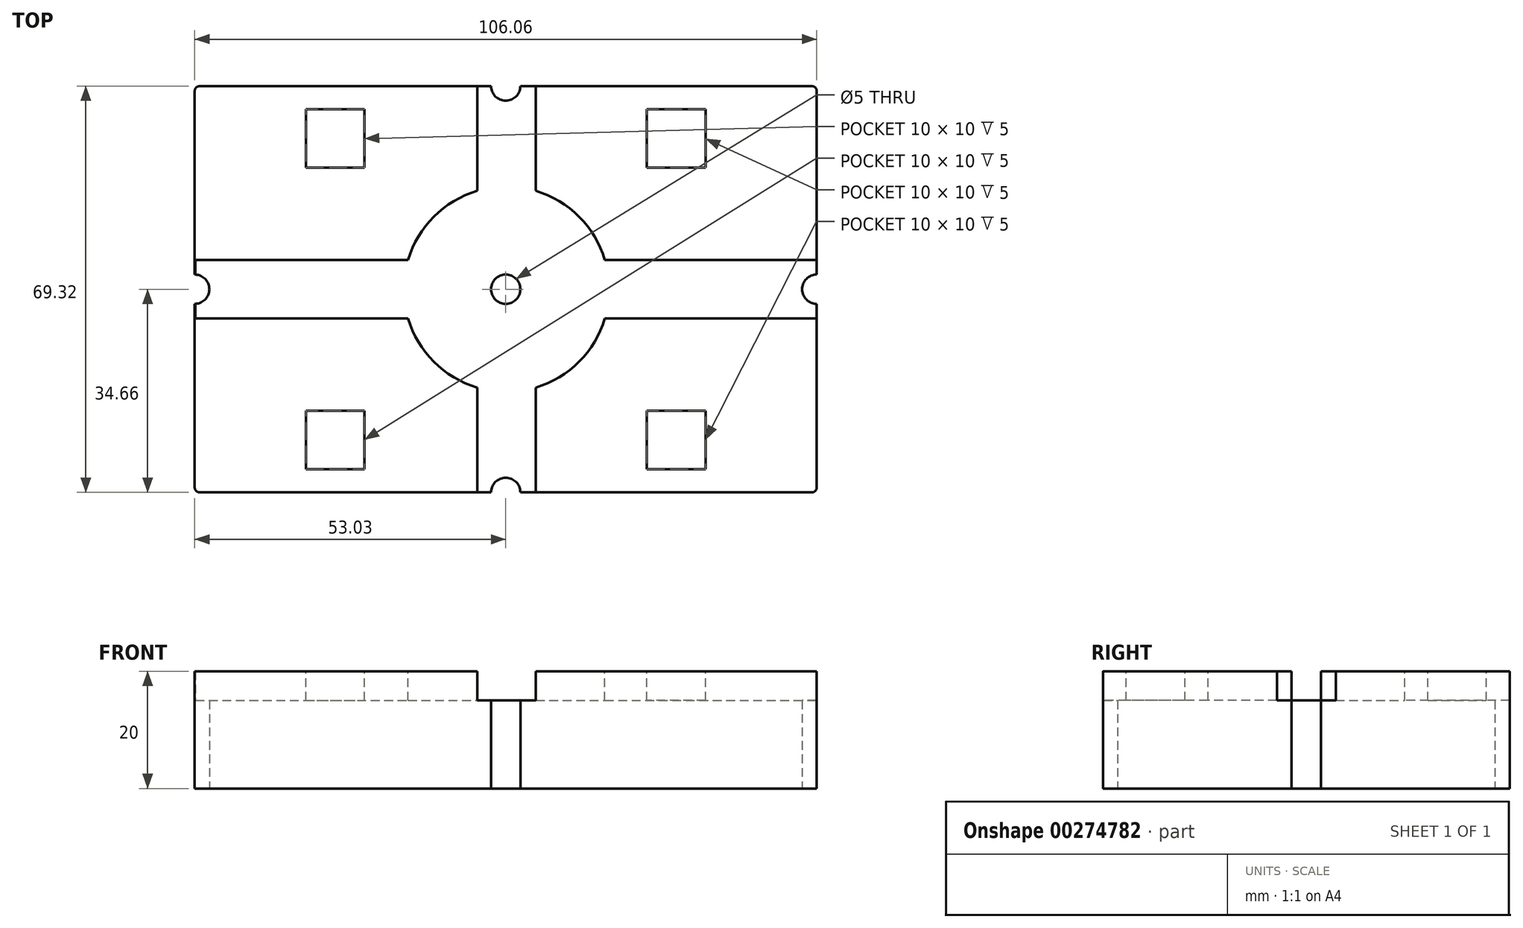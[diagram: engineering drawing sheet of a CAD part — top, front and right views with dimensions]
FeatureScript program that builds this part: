
annotation { "Feature Type Name" : "Feature", "Feature Type Description" : "" }
export const myFeature = defineFeature(function(context is Context, id is Id, definition is map)
    precondition{}
    {
        {
            var Q0;
            Q0=qCreatedBy(makeId("Top.planeOp"),FACE);
            var sketch = newSketch(context, id + "F0", { "sketchPlane" : qUnion([Q0])});
            skLineSegment(sketch, "E0.bottom", {"start": v(53.03, -34.66) * mm, "end": v(-53.03, -34.66) * mm});
            skLineSegment(sketch, "E0.top", {"start": v(53.03, 34.66) * mm, "end": v(-53.03, 34.66) * mm});
            skLineSegment(sketch, "E0.left", {"start": v(53.03, -34.66) * mm, "end": v(53.03, 34.66) * mm});
            skLineSegment(sketch, "E0.right", {"start": v(-53.03, -34.66) * mm, "end": v(-53.03, 34.66) * mm});
            skPoint(sketch, "E0.middle", {"position": v(0, 0) * mm});
            skLineSegment(sketch, "E1", {"start": v(-5, 0) * mm, "end": v(0, 0) * mm, "construction": true});
            skLineSegment(sketch, "E2.0", {"start": v(-53.03, -5) * mm, "end": v(-16.77, -5) * mm});
            skLineSegment(sketch, "E3.0", {"start": v(-53.03, 5) * mm, "end": v(-16.77, 5) * mm});
            skLineSegment(sketch, "E4", {"start": v(0, 5) * mm, "end": v(0, -5) * mm, "construction": true});
            skLineSegment(sketch, "E5.0", {"start": v(5, 34.66) * mm, "end": v(5, 16.77) * mm});
            skLineSegment(sketch, "E6.0", {"start": v(-5, 34.66) * mm, "end": v(-5, 16.77) * mm});
            skPoint(sketch, "E7.orphan", {"position": v(-53.03, 0) * mm});
            skLineSegment(sketch, "E8.trimOffspring", {"start": v(-5, -16.77) * mm, "end": v(-5, -34.66) * mm});
            skPoint(sketch, "E9.orphan", {"position": v(0, 34.66) * mm});
            skLineSegment(sketch, "E10.trimOffspring", {"start": v(5, -16.77) * mm, "end": v(5, -34.66) * mm});
            skLineSegment(sketch, "E11.trimOffspring", {"start": v(16.77, 5) * mm, "end": v(53.03, 5) * mm});
            skPoint(sketch, "E12.orphan", {"position": v(0, -34.66) * mm});
            skLineSegment(sketch, "E13.trimOffspring", {"start": v(16.77, -5) * mm, "end": v(53.03, -5) * mm});
            skPoint(sketch, "E14.orphan", {"position": v(53.03, 0) * mm});
            skCircle(sketch, "E15", {"center": v(0, 0) * mm, "radius": 17.5 * mm});
            skSolve(sketch);
        }
        {
            var Q0;
            {var subQ0=sQuery(id+"F0.wireOp",EDGE,"E5.0");Q0=makeQuery(id+"F0.imprint","IMPRINT",FACE,{"disambiguationData":[TD([[makeQuery(id+"F0.imprint","IMPRINT",EDGE,{"derivedFrom":subQ0}),1.0]])]});}
            var Q1;
            {var subQ0=sQuery(id+"F0.wireOp",EDGE,"E5.0");Q1=makeQuery(id+"F0.imprint","IMPRINT",FACE,{"disambiguationData":[TD([[makeQuery(id+"F0.imprint","IMPRINT",EDGE,{"derivedFrom":subQ0}),-1.0]])]});}
            var Q2;
            {var subQ1=sQuery(id+"F0.wireOp",EDGE,"E3.0");Q2=makeQuery(id+"F0.imprint","IMPRINT",FACE,{"disambiguationData":[TD([[makeQuery(id+"F0.imprint","IMPRINT",EDGE,{"derivedFrom":subQ1}),1.0]])]});}
            var Q3;
            {var subQ0=sQuery(id+"F0.wireOp",EDGE,"E2.0");Q3=makeQuery(id+"F0.imprint","IMPRINT",FACE,{"disambiguationData":[TD([[makeQuery(id+"F0.imprint","IMPRINT",EDGE,{"derivedFrom":subQ0}),-1.0]])]});}
            var Q4;
            {var subQ4=sQuery(id+"F0.wireOp",EDGE,"E10.trimOffspring");Q4=makeQuery(id+"F0.imprint","IMPRINT",FACE,{"disambiguationData":[TD([[makeQuery(id+"F0.imprint","IMPRINT",EDGE,{"derivedFrom":subQ4}),1.0]])]});}
            var Q5;
            {var subQ0=sQuery(id+"F0.wireOp",EDGE,"E11.trimOffspring");Q5=makeQuery(id+"F0.imprint","IMPRINT",FACE,{"disambiguationData":[TD([[makeQuery(id+"F0.imprint","IMPRINT",EDGE,{"derivedFrom":subQ0}),-1.0]])]});}
            var Q6;
            {var subQ0=sQuery(id+"F0.wireOp",EDGE,"E15");var subQ4=makeQuery(id+"F0.imprint","INTERSECT",VERTEX,{"derivedFrom":[sQuery(id+"F0.wireOp",EDGE,"E5.0"),subQ0]});Q6=makeQuery(id+"F0.imprint","IMPRINT",FACE,{"disambiguationData":[TD([[makeQuery(id+"F0.imprint","IMPRINT",EDGE,{"disambiguationData":[TD([[subQ4,1.0]])],"derivedFrom":subQ0}),1.0]])]});}
            var Q7;
            {var subQ0=sQuery(id+"F0.wireOp",EDGE,"E2.0");Q7=makeQuery(id+"F0.imprint","IMPRINT",FACE,{"disambiguationData":[TD([[makeQuery(id+"F0.imprint","IMPRINT",EDGE,{"derivedFrom":subQ0}),1.0]])]});}
            var Q8;
            {var subQ0=sQuery(id+"F0.wireOp",EDGE,"E8.trimOffspring");Q8=makeQuery(id+"F0.imprint","IMPRINT",FACE,{"disambiguationData":[TD([[makeQuery(id+"F0.imprint","IMPRINT",EDGE,{"derivedFrom":subQ0}),1.0]])]});}
            extrude(context, id + "F1", {"entities" : qUnion([Q0, Q1, Q2, Q3, Q4, Q5, Q6, Q7, Q8]), "depth" : 20 * mm});
        }
        {
            var Q0;
            Q0=makeQuery(id+"F1.opExtrude","CAP_FACE",FACE,{"disambiguationData":[OSD([sQuery(id+"F0.wireOp",EDGE,"E0.bottom"),sQuery(id+"F0.wireOp",EDGE,"E0.top"),sQuery(id+"F0.wireOp",EDGE,"E0.left"),sQuery(id+"F0.wireOp",EDGE,"E0.right")])],"isStart":false});
            var sketch = newSketch(context, id + "F2", { "sketchPlane" : qUnion([Q0])});
            skLineSegment(sketch, "E16.bottom", {"start": v(53.15, -34.66) * mm, "end": v(-52.9, -34.66) * mm});
            skLineSegment(sketch, "E16.top", {"start": v(53.15, 34.66) * mm, "end": v(-52.9, 34.66) * mm});
            skLineSegment(sketch, "E16.left", {"start": v(53.15, -34.66) * mm, "end": v(53.15, 34.66) * mm});
            skLineSegment(sketch, "E16.right", {"start": v(-52.9, -34.66) * mm, "end": v(-52.9, 34.66) * mm});
            skPoint(sketch, "E16.middle", {"position": v(0.12, 0) * mm});
            skLineSegment(sketch, "E17", {"start": v(-4.87, 0) * mm, "end": v(0.12, 0) * mm, "construction": true});
            skLineSegment(sketch, "E18.0", {"start": v(-52.9, -5) * mm, "end": v(-16.65, -5) * mm});
            skLineSegment(sketch, "E19.0", {"start": v(-52.9, 5) * mm, "end": v(-16.65, 5) * mm});
            skLineSegment(sketch, "E20", {"start": v(0.12, 5) * mm, "end": v(0.12, -5) * mm, "construction": true});
            skLineSegment(sketch, "E21.0", {"start": v(5.12, 34.66) * mm, "end": v(5.12, 16.77) * mm});
            skLineSegment(sketch, "E22.0", {"start": v(-4.88, 34.66) * mm, "end": v(-4.88, 16.77) * mm});
            skPoint(sketch, "E23.orphan", {"position": v(-52.9, 0) * mm});
            skLineSegment(sketch, "E24.trimOffspring", {"start": v(-4.88, -16.77) * mm, "end": v(-4.88, -34.66) * mm});
            skPoint(sketch, "E25.orphan", {"position": v(0.12, 34.66) * mm});
            skLineSegment(sketch, "E26.trimOffspring", {"start": v(5.12, -16.77) * mm, "end": v(5.12, -34.66) * mm});
            skLineSegment(sketch, "E27.trimOffspring", {"start": v(16.9, 5) * mm, "end": v(53.15, 5) * mm});
            skPoint(sketch, "E28.orphan", {"position": v(0.12, -34.66) * mm});
            skLineSegment(sketch, "E29.trimOffspring", {"start": v(16.9, -5) * mm, "end": v(53.15, -5) * mm});
            skPoint(sketch, "E30.orphan", {"position": v(53.15, 0) * mm});
            skCircle(sketch, "E31", {"center": v(0.12, 0) * mm, "radius": 17.5 * mm});
            skSolve(sketch);
        }
        {
            var Q0;
            {var subQ0=sQuery(id+"F2.wireOp",EDGE,"E18.0");Q0=makeQuery(id+"F2.imprint","IMPRINT",FACE,{"disambiguationData":[TD([[makeQuery(id+"F2.imprint","IMPRINT",EDGE,{"derivedFrom":subQ0}),1.0]])]});}
            var Q1;
            {var subQ0=sQuery(id+"F2.wireOp",EDGE,"E21.0");Q1=makeQuery(id+"F2.imprint","IMPRINT",FACE,{"disambiguationData":[TD([[makeQuery(id+"F2.imprint","IMPRINT",EDGE,{"derivedFrom":subQ0}),-1.0]])]});}
            var Q2;
            {var subQ0=sQuery(id+"F2.wireOp",EDGE,"E31");var subQ5=makeQuery(id+"F2.imprint","INTERSECT",VERTEX,{"derivedFrom":[sQuery(id+"F2.wireOp",EDGE,"E21.0"),subQ0]});Q2=makeQuery(id+"F2.imprint","IMPRINT",FACE,{"disambiguationData":[TD([[makeQuery(id+"F2.imprint","IMPRINT",EDGE,{"disambiguationData":[TD([[subQ5,1.0]])],"derivedFrom":subQ0}),1.0]])]});}
            var Q3;
            {var subQ0=sQuery(id+"F2.wireOp",EDGE,"E31");var subQ1=sQuery(id+"F2.wireOp",EDGE,"E27.trimOffspring");var subQ2=makeQuery(id+"F2.imprint","INTERSECT",VERTEX,{"derivedFrom":[subQ1,subQ0]});Q3=makeQuery(id+"F2.imprint","IMPRINT",FACE,{"disambiguationData":[TD([[makeQuery(id+"F2.imprint","IMPRINT",EDGE,{"disambiguationData":[TD([[subQ2,-1.0]])],"derivedFrom":subQ1}),-1.0]])]});}
            var Q4;
            {var subQ0=sQuery(id+"F2.wireOp",EDGE,"E24.trimOffspring");Q4=makeQuery(id+"F2.imprint","IMPRINT",FACE,{"disambiguationData":[TD([[makeQuery(id+"F2.imprint","IMPRINT",EDGE,{"derivedFrom":subQ0}),1.0]])]});}
            extrude(context, id + "F3", {"entities" : qUnion([Q0, Q1, Q2, Q3, Q4]), "operationType" : NewBodyOperationType.REMOVE, "oppositeDirection" : true, "depth" : 5 * mm});
        }
        {
            var Q0;
            {var subQ1=sQuery(id+"F2.wireOp",EDGE,"E21.0");var subQ2=sQuery(id+"F0.wireOp",EDGE,"E0.left");var subQ3=sQuery(id+"F0.wireOp",EDGE,"E0.top");Q0=makeQuery(id+"F3.boolean.opBoolean","SPLIT",FACE,{"disambiguationData":[TD([makeQuery(id+"F3.opExtrude","SWEPT_FACE",FACE,{"disambiguationData":[OSD([subQ1])]})])],"derivedFrom":makeQuery(id+"F1.opExtrude","CAP_FACE",FACE,{"disambiguationData":[OSD([sQuery(id+"F0.wireOp",EDGE,"E0.bottom"),subQ3,subQ2,sQuery(id+"F0.wireOp",EDGE,"E0.right")])],"isStart":false})});}
            var sketch = newSketch(context, id + "F4", { "sketchPlane" : qUnion([Q0])});
            skLineSegment(sketch, "E32.bottom", {"start": v(34.08, 20.71) * mm, "end": v(24.08, 20.71) * mm});
            skLineSegment(sketch, "E32.top", {"start": v(34.08, 30.71) * mm, "end": v(24.08, 30.71) * mm});
            skLineSegment(sketch, "E32.left", {"start": v(34.08, 20.71) * mm, "end": v(34.08, 30.71) * mm});
            skLineSegment(sketch, "E32.right", {"start": v(24.08, 20.71) * mm, "end": v(24.08, 30.71) * mm});
            skPoint(sketch, "E32.middle", {"position": v(29.08, 25.71) * mm});
            skPoint(sketch, "E32.middle.positionSnap0", {"position": v(29.08, 34.66) * mm});
            skPoint(sketch, "E32.middle.positionSnap1", {"position": v(5.12, 25.71) * mm});
            skPoint(sketch, "E32.centerSnap0", {"position": v(29.08, 34.66) * mm});
            skPoint(sketch, "E32.centerSnap1", {"position": v(5.12, 25.71) * mm});
            skLineSegment(sketch, "E33.MirrorCS", {"start": v(-34.08, 30.71) * mm, "end": v(-24.08, 30.71) * mm});
            skLineSegment(sketch, "E34.MirrorCS", {"start": v(-24.08, 20.71) * mm, "end": v(-24.08, 30.71) * mm});
            skLineSegment(sketch, "E35.MirrorCS", {"start": v(-34.08, 20.71) * mm, "end": v(-24.08, 20.71) * mm});
            skLineSegment(sketch, "E36.MirrorCS", {"start": v(-34.08, 20.71) * mm, "end": v(-34.08, 30.71) * mm});
            skLineSegment(sketch, "E37", {"start": v(-53.34, 0) * mm, "end": v(53.57, 0) * mm, "construction": true});
            skLineSegment(sketch, "E38.MirrorCS", {"start": v(34.08, -30.71) * mm, "end": v(24.08, -30.71) * mm});
            skLineSegment(sketch, "E39.MirrorCS", {"start": v(34.08, -20.71) * mm, "end": v(24.08, -20.71) * mm});
            skLineSegment(sketch, "E40.MirrorCS", {"start": v(34.08, -20.71) * mm, "end": v(34.08, -30.71) * mm});
            skLineSegment(sketch, "E41.MirrorCS", {"start": v(24.08, -20.71) * mm, "end": v(24.08, -30.71) * mm});
            skLineSegment(sketch, "E42.MirrorCS", {"start": v(-34.08, -30.71) * mm, "end": v(-24.08, -30.71) * mm});
            skLineSegment(sketch, "E43.MirrorCS", {"start": v(-34.08, -20.71) * mm, "end": v(-24.08, -20.71) * mm});
            skLineSegment(sketch, "E44.MirrorCS", {"start": v(-24.08, -20.71) * mm, "end": v(-24.08, -30.71) * mm});
            skLineSegment(sketch, "E45.MirrorCS", {"start": v(-34.08, -20.71) * mm, "end": v(-34.08, -30.71) * mm});
            skSolve(sketch);
        }
        {
            var Q0;
            Q0=makeQuery(id+"F4.imprint","IMPRINT",FACE,{"disambiguationData":[TD([[makeQuery(id+"F4.imprint","IMPRINT",EDGE,{"derivedFrom":sQuery(id+"F4.wireOp",EDGE,"E33.MirrorCS")}),-1.0]])]});
            var Q1;
            Q1=makeQuery(id+"F4.imprint","IMPRINT",FACE,{"disambiguationData":[TD([[makeQuery(id+"F4.imprint","IMPRINT",EDGE,{"derivedFrom":sQuery(id+"F4.wireOp",EDGE,"E32.bottom")}),-1.0]])]});
            var Q2;
            Q2=makeQuery(id+"F4.imprint","IMPRINT",FACE,{"disambiguationData":[TD([[makeQuery(id+"F4.imprint","IMPRINT",EDGE,{"derivedFrom":sQuery(id+"F4.wireOp",EDGE,"E38.MirrorCS")}),-1.0]])]});
            var Q3;
            Q3=makeQuery(id+"F4.imprint","IMPRINT",FACE,{"disambiguationData":[TD([[makeQuery(id+"F4.imprint","IMPRINT",EDGE,{"derivedFrom":sQuery(id+"F4.wireOp",EDGE,"E42.MirrorCS")}),1.0]])]});
            extrude(context, id + "F5", {"entities" : qUnion([Q0, Q1, Q2, Q3]), "operationType" : NewBodyOperationType.REMOVE, "oppositeDirection" : true, "depth" : 5 * mm});
        }
        {
            var Q0;
            Q0=sQuery(id+"F0.wireOp",VERTEX,"E12.orphan");
            var Q1;
            Q1=sQuery(id+"F0.wireOp",VERTEX,"E9.orphan");
            var Q2;
            Q2=sQuery(id+"F0.wireOp",VERTEX,"E7.orphan");
            var Q3;
            Q3=sQuery(id+"F0.wireOp",VERTEX,"E0.middle");
            var Q4;
            Q4=makeQuery(id+"F1.opExtrude","SWEPT_BODY",BODY,{"disambiguationData":[OSD([sQuery(id+"F0.wireOp",EDGE,"E0.bottom"),sQuery(id+"F0.wireOp",EDGE,"E0.top"),sQuery(id+"F0.wireOp",EDGE,"E0.left"),sQuery(id+"F0.wireOp",EDGE,"E0.right")])]});
            hole(context, id + "F6", {"style" : HoleStyle.SIMPLE, "endStyle" : HoleEndStyle.THROUGH, "oppositeDirection" : true, "holeDiameter" : 5 * mm, "tappedDepth" : 12 * mm, "tapClearance" : 3, "locations" : qUnion([Q0, Q1, Q2, Q3]), "scope" : qUnion([Q4])});
        }
        {
            var Q0;
            Q0=sQuery(id+"F0.wireOp",VERTEX,"E14.orphan");
            var Q1;
            Q1=makeQuery(id+"F1.opExtrude","SWEPT_BODY",BODY,{"disambiguationData":[OSD([sQuery(id+"F0.wireOp",EDGE,"E0.bottom"),sQuery(id+"F0.wireOp",EDGE,"E0.top"),sQuery(id+"F0.wireOp",EDGE,"E0.left"),sQuery(id+"F0.wireOp",EDGE,"E0.right")])]});
            hole(context, id + "F7", {"style" : HoleStyle.SIMPLE, "endStyle" : HoleEndStyle.THROUGH, "oppositeDirection" : true, "holeDiameter" : 5 * mm, "tappedDepth" : 12 * mm, "tapClearance" : 3, "locations" : qUnion([Q0]), "scope" : qUnion([Q1])});
        }
        {
            var Q0;
            Q0=makeQuery(id+"F1.opExtrude","SWEPT_EDGE",EDGE,{"disambiguationData":[OSD([sQuery(id+"F0.wireOp",EDGE,"E0.bottom"),sQuery(id+"F0.wireOp",EDGE,"E0.left")])]});
            var Q1;
            Q1=makeQuery(id+"F1.opExtrude","SWEPT_EDGE",EDGE,{"disambiguationData":[OSD([sQuery(id+"F0.wireOp",EDGE,"E0.top"),sQuery(id+"F0.wireOp",EDGE,"E0.left")])]});
            var Q2;
            Q2=makeQuery(id+"F1.opExtrude","SWEPT_EDGE",EDGE,{"disambiguationData":[OSD([sQuery(id+"F0.wireOp",EDGE,"E0.bottom"),sQuery(id+"F0.wireOp",EDGE,"E0.right")])]});
            var Q3;
            Q3=makeQuery(id+"F1.opExtrude","SWEPT_EDGE",EDGE,{"disambiguationData":[OSD([sQuery(id+"F0.wireOp",EDGE,"E0.top"),sQuery(id+"F0.wireOp",EDGE,"E0.right")])]});
            fillet(context, id + "F8", {"entities" : qUnion([Q0, Q1, Q2, Q3]), "radius" : 1 * mm, "tangentPropagation" : true, "rho" : 0.5, "crossSection" : FilletCrossSection.CONIC, "allowEdgeOverflow" : false});
        }
    });
